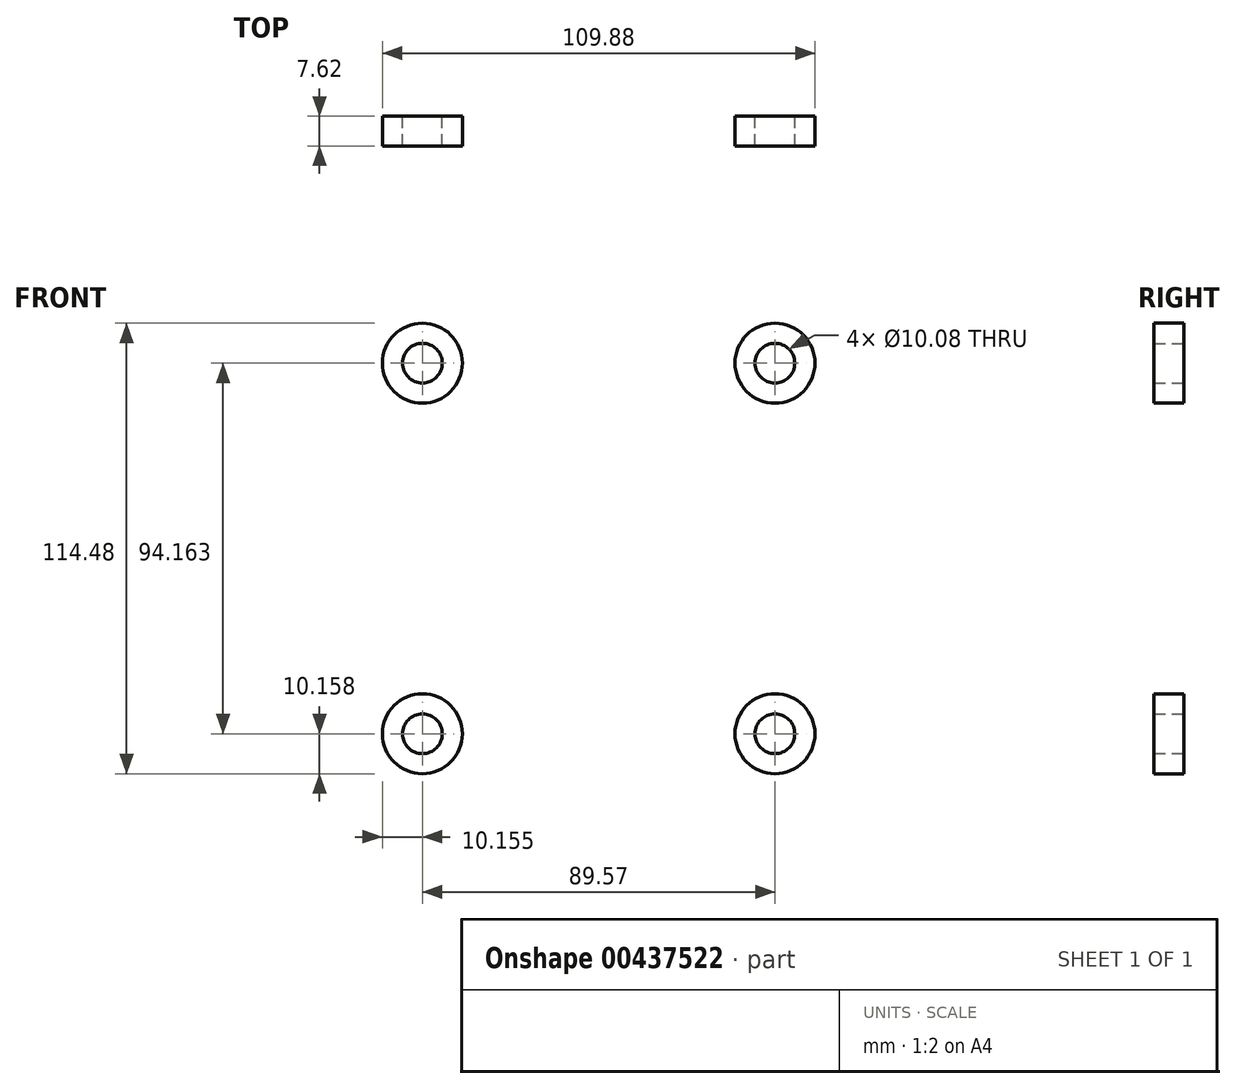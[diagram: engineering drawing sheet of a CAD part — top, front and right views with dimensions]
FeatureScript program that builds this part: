
annotation { "Feature Type Name" : "Feature", "Feature Type Description" : "" }
export const myFeature = defineFeature(function(context is Context, id is Id, definition is map)
    precondition{}
    {
        {
            var Q0;
            Q0=qCreatedBy(makeId("Front.planeOp"),FACE);
            var sketch = newSketch(context, id + "F0", { "sketchPlane" : qUnion([Q0])});
            skCircle(sketch, "E0", {"center": v(-44.78, 47.08) * mm, "radius": 5.04 * mm});
            skCircle(sketch, "E1", {"center": v(-44.78, 47.08) * mm, "radius": 10.16 * mm});
            skCircle(sketch, "E2.MirrorC", {"center": v(44.78, 47.08) * mm, "radius": 10.16 * mm});
            skCircle(sketch, "E3.MirrorC", {"center": v(44.78, 47.08) * mm, "radius": 5.04 * mm});
            skCircle(sketch, "E4.MirrorC", {"center": v(-44.78, -47.08) * mm, "radius": 10.16 * mm});
            skCircle(sketch, "E5.MirrorC", {"center": v(-44.78, -47.08) * mm, "radius": 5.04 * mm});
            skCircle(sketch, "E6.MirrorC", {"center": v(44.78, -47.08) * mm, "radius": 10.16 * mm});
            skCircle(sketch, "E7.MirrorC", {"center": v(44.78, -47.08) * mm, "radius": 5.04 * mm});
            skSolve(sketch);
        }
        {
            var Q0;
            Q0 = qSketchRegion(id + "F0", true);
            extrude(context, id + "F1", {"entities" : qUnion([Q0]), "depth" : 7.62 * mm});
        }
    });
